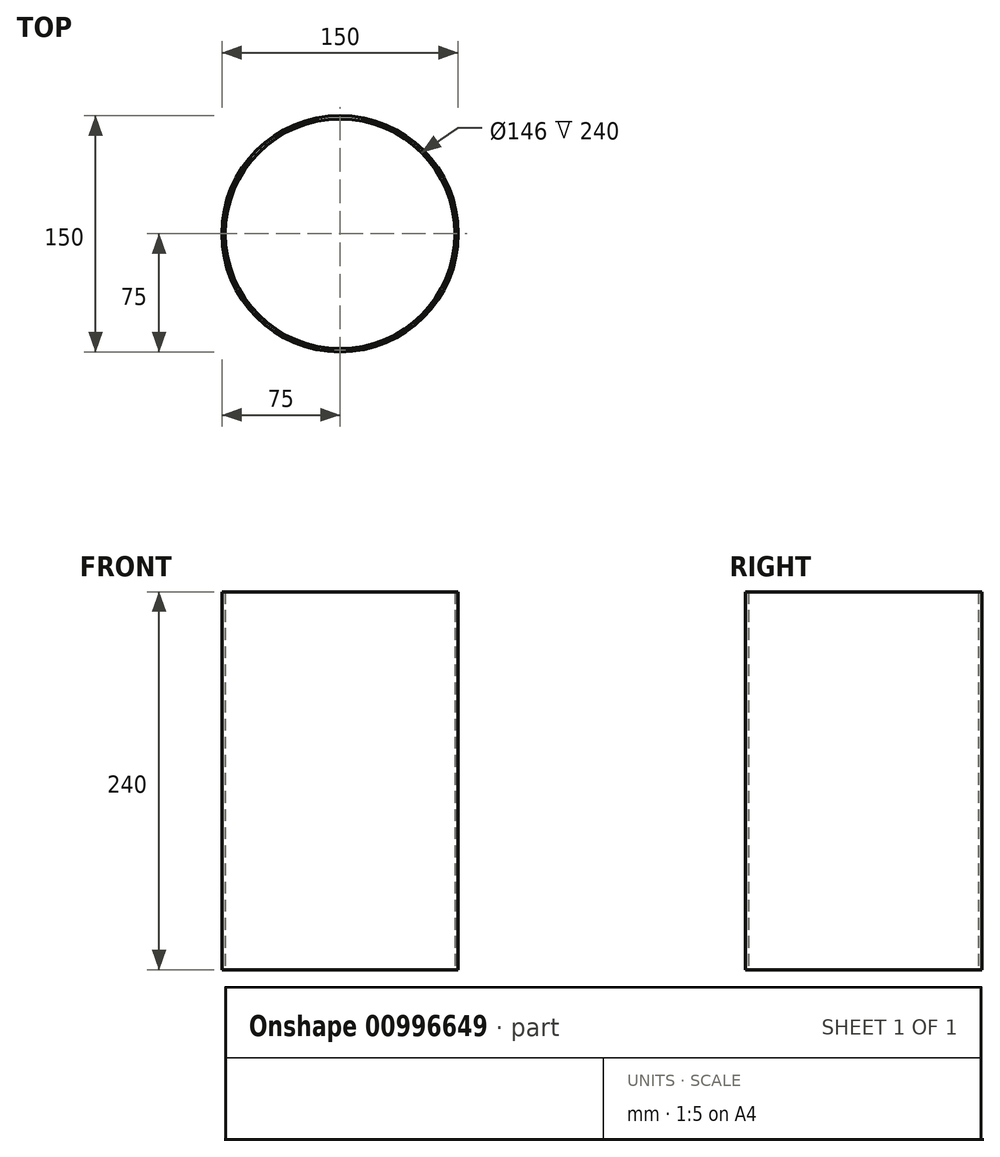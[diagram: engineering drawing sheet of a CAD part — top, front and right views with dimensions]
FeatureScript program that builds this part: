
annotation { "Feature Type Name" : "Feature", "Feature Type Description" : "" }
export const myFeature = defineFeature(function(context is Context, id is Id, definition is map)
    precondition{}
    {
        {
            var Q0;
            Q0=qCreatedBy(makeId("Top.planeOp"),FACE);
            var sketch = newSketch(context, id + "F0", { "sketchPlane" : qUnion([Q0])});
            skCircle(sketch, "E0", {"center": v(0, 0) * mm, "radius": 73 * mm});
            skCircle(sketch, "E1", {"center": v(0, 0) * mm, "radius": 75 * mm});
            skSolve(sketch);
        }
        {
            var Q0;
            Q0 = qSketchRegion(id + "F0", true);
            extrude(context, id + "F1", {"entities" : qUnion([Q0]), "depth" : 240 * mm, "offsetDistance" : 25 * mm});
        }
    });
